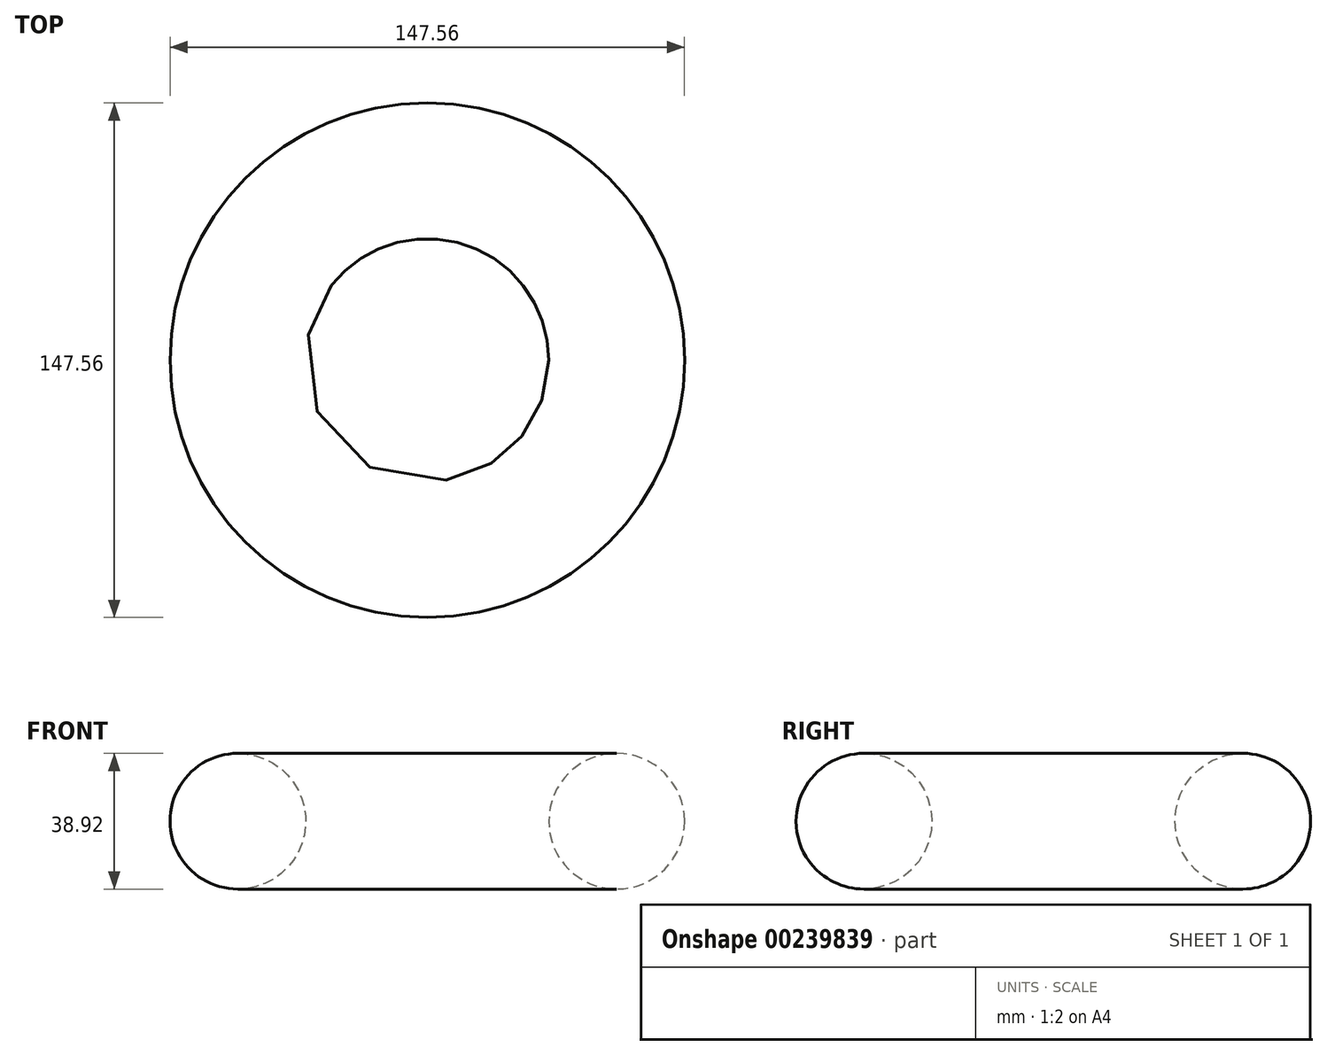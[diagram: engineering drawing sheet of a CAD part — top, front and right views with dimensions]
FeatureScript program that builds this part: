
annotation { "Feature Type Name" : "Feature", "Feature Type Description" : "" }
export const myFeature = defineFeature(function(context is Context, id is Id, definition is map)
    precondition{}
    {
        {
            var Q0;
            Q0=qCreatedBy(makeId("Front.planeOp"),FACE);
            var sketch = newSketch(context, id + "F0", { "sketchPlane" : qUnion([Q0])});
            skCircle(sketch, "E0", {"center": v(-54.32, 46.7) * mm, "radius": 19.46 * mm});
            skLineSegment(sketch, "E1", {"start": v(0, 75.44) * mm, "end": v(0, 0) * mm});
            skLineSegment(sketch, "E2", {"start": v(0, 75.44) * mm, "end": v(0, 0) * mm, "construction": true});
            skSolve(sketch);
        }
        {
            var Q0;
            Q0=makeQuery(id+"F0.imprint","IMPRINT",FACE,{"disambiguationData":[TD([[makeQuery(id+"F0.imprint","IMPRINT",EDGE,{"derivedFrom":sQuery(id+"F0.wireOp",EDGE,"E0")}),1.0]])]});
            var Q1;
            Q1=sQuery(id+"F0.wireOp",EDGE,"E1");
            revolve(context, id + "F1", {"entities" : qUnion([Q0]), "axis" : qUnion([Q1]), "revolveType" : RevolveType.FULL});
        }
    });
